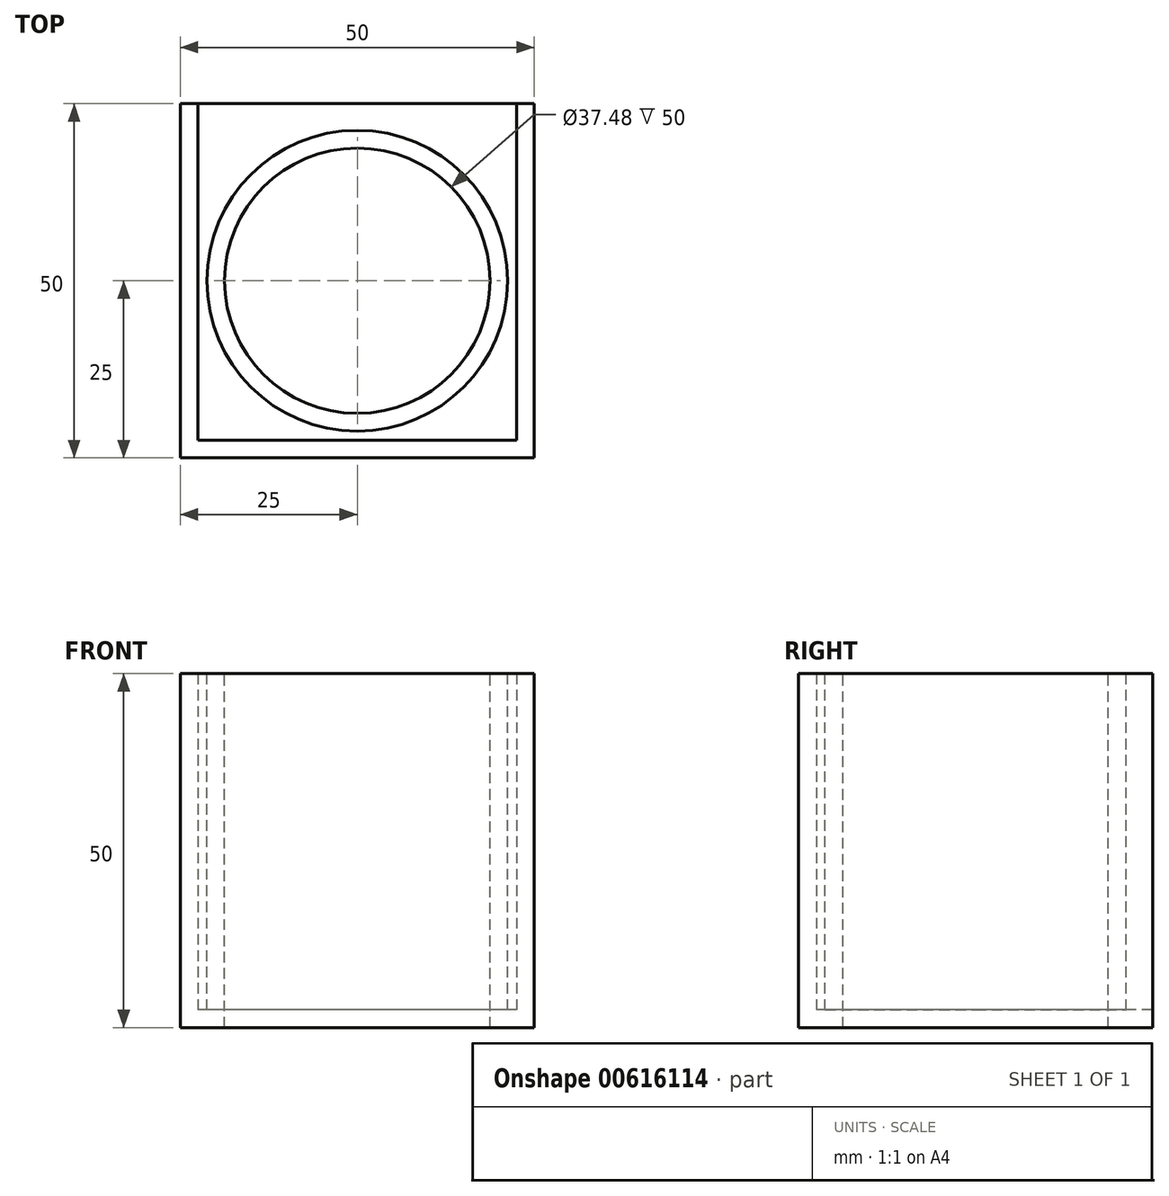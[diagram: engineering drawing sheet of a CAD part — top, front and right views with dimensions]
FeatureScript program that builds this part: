
annotation { "Feature Type Name" : "Feature", "Feature Type Description" : "" }
export const myFeature = defineFeature(function(context is Context, id is Id, definition is map)
    precondition{}
    {
        {
            var Q0;
            Q0=qCreatedBy(makeId("Top.planeOp"),FACE);
            var sketch = newSketch(context, id + "F0", { "sketchPlane" : qUnion([Q0])});
            skLineSegment(sketch, "E0.bottom", {"start": v(25, 25) * mm, "end": v(-25, 25) * mm});
            skLineSegment(sketch, "E0.top", {"start": v(25, -25) * mm, "end": v(-25, -25) * mm});
            skLineSegment(sketch, "E0.left", {"start": v(25, 25) * mm, "end": v(25, -25) * mm});
            skLineSegment(sketch, "E0.right", {"start": v(-25, 25) * mm, "end": v(-25, -25) * mm});
            skPoint(sketch, "E0.middle", {"position": v(0, 0) * mm});
            skSolve(sketch);
        }
        {
            var Q0;
            Q0 = qSketchRegion(id + "F0", true);
            extrude(context, id + "F1", {"entities" : qUnion([Q0]), "depth" : 50 * mm, "offsetDistance" : 25 * mm});
        }
        {
            var Q0;
            Q0=makeQuery(id+"F1.opExtrude","CAP_FACE",FACE,{"disambiguationData":[OSD([sQuery(id+"F0.wireOp",EDGE,"E0.bottom"),sQuery(id+"F0.wireOp",EDGE,"E0.top"),sQuery(id+"F0.wireOp",EDGE,"E0.left"),sQuery(id+"F0.wireOp",EDGE,"E0.right")])],"isStart":false});
            var sketch = newSketch(context, id + "F2", { "sketchPlane" : qUnion([Q0])});
            skCircle(sketch, "E1", {"center": v(0, 0) * mm, "radius": 18.74 * mm});
            skSolve(sketch);
        }
        {
            var Q0;
            Q0=makeQuery(id+"F2.imprint","IMPRINT",FACE,{"disambiguationData":[TD([[makeQuery(id+"F2.imprint","IMPRINT",EDGE,{"derivedFrom":sQuery(id+"F2.wireOp",EDGE,"E1")}),1.0]])]});
            extrude(context, id + "F3", {"entities" : qUnion([Q0]), "operationType" : NewBodyOperationType.REMOVE, "oppositeDirection" : true, "depth" : 50 * mm, "offsetDistance" : 25 * mm});
        }
        {
            var Q0;
            Q0=makeQuery(id+"F1.opExtrude","CAP_FACE",FACE,{"disambiguationData":[OSD([sQuery(id+"F0.wireOp",EDGE,"E0.bottom"),sQuery(id+"F0.wireOp",EDGE,"E0.top"),sQuery(id+"F0.wireOp",EDGE,"E0.left"),sQuery(id+"F0.wireOp",EDGE,"E0.right")])],"isStart":false});
            var Q1;
            Q1=makeQuery(id+"F1.opExtrude","SWEPT_FACE",FACE,{"disambiguationData":[OSD([sQuery(id+"F0.wireOp",EDGE,"E0.bottom")])]});
            shell(context, id + "F4", {"entities" : qUnion([Q0, Q1]), "thickness" : 2.5 * mm});
        }
    });
